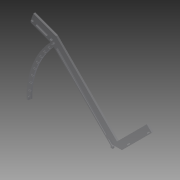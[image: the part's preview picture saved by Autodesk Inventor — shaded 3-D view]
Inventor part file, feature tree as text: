
AUTODESK INVENTOR PART (.ipt)
format: ipt  version: 2013 (Build 170138000, 138)  size: 276,992 bytes
history: native  units: in
note: dims shown in document units (in); Inventor stores cm internally (conversion verified against a paired STEP export)
features: reference x12, extrude x9, sketch x9
ambient origin geometry x8: Origin, YZ Plane, XZ Plane, XY Plane, X Axis, Y Axis, Z Axis, Center Point
bodies: Solid1 (feature_tree)
feature tree (30):
  extrude  "Extrusion1"  Depth=0.25in TaperAngle=0.0deg
  extrude  "Extrusion2"  Depth=0.25in
  extrude  "Extrusion3"  Depth=0.25in TaperAngle=0.0deg
  extrude  "Extrusion4"  Depth=1.0in
  extrude  "Extrusion7"  Depth=0.25in TaperAngle=0.0deg
  extrude  "Extrusion8"  Depth=1.375in
  extrude  "Extrusion11"  Depth=6.0in
  extrude  "Extrusion12"  Depth=0.125in
  extrude  "Extrusion13"  Depth=0.25in
  sketch  "Sketch1"  dims[d0=23.375in d1=0.25in d2=0.0in]
  sketch  "Sketch2"  dims[d3=0.25in d4=0.25in]
  sketch  "Sketch3"  dims[d5=0.25in d6=0.0in d10=0.25in d11=0.0in]
  reference  "Reference1"
  sketch  "Sketch4"  dims[d12=0.25in d13=0.0in d19=1.0in]
  reference  "Reference2"
  sketch  "Sketch7"  dims[d20=0.7043in d21=0.25in d22=0.0in]
  reference  "Reference5"
  reference  "Reference6"
  reference  "Reference7"
  reference  "Reference8"
  sketch  "Sketch8"  dims[d23=0.25in d24=0.0in d35=1.375in]
  reference  "Reference9"
  reference  "Reference10"
  reference  "Reference11"
  reference  "Reference12"
  reference  "Reference13"
  sketch  "Sketch11"  dims[d36=0.25in d37=0.0in d38=6.0in]
  sketch  "Sketch12"  dims[d39=1.0in d40=0.125in]
  sketch  "Sketch13"  dims[d41=0.5in d42=0.25in d43=0.125in d44=0.125in d45=0.5in d46=0.125in d47=0.125in d48=3.5in d49=0.25in d50=0.0in d51=1.0in d52=0.0in]
  reference  "Reference14"
